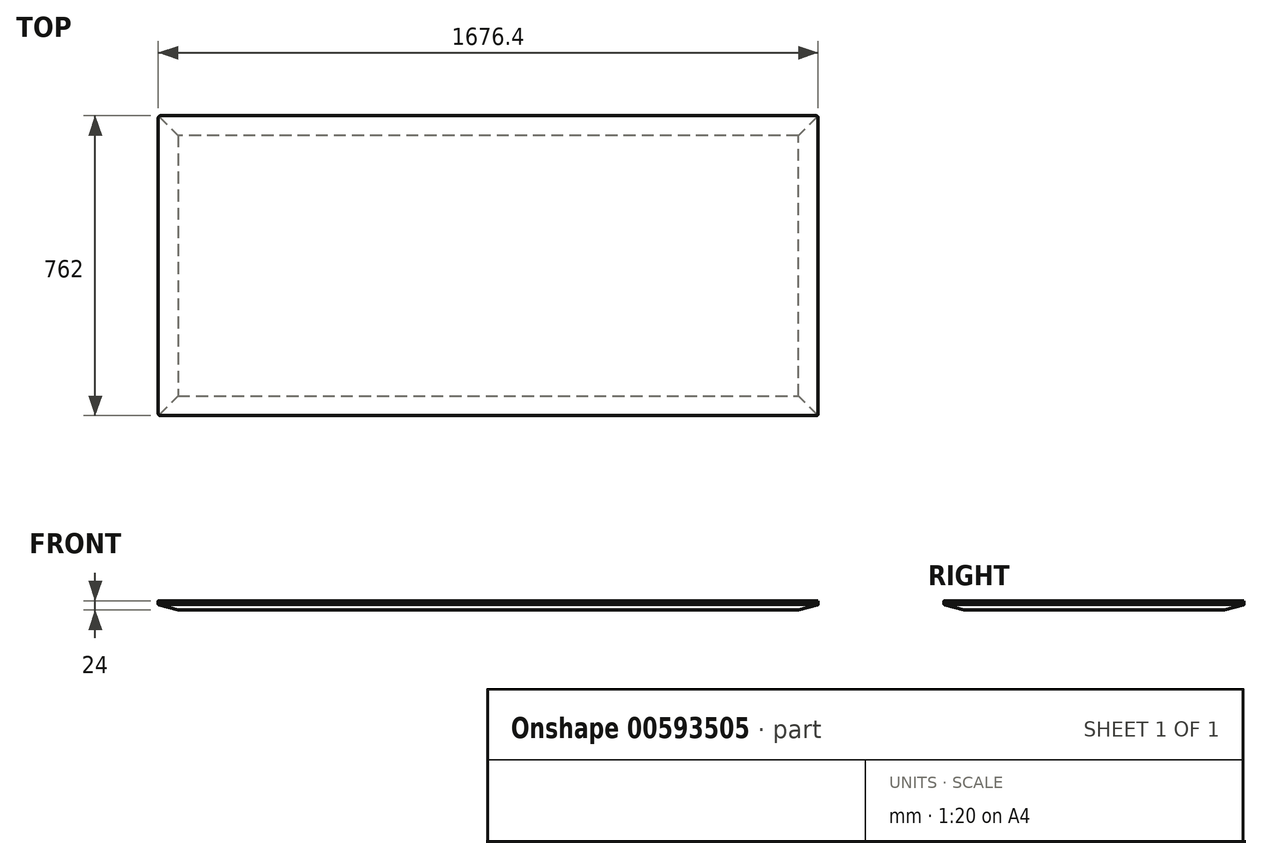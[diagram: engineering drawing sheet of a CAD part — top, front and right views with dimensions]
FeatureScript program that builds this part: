
annotation { "Feature Type Name" : "Feature", "Feature Type Description" : "" }
export const myFeature = defineFeature(function(context is Context, id is Id, definition is map)
    precondition{}
    {
        {
            var Q0;
            Q0=qCreatedBy(makeId("Top.planeOp"),FACE);
            var sketch = newSketch(context, id + "F0", { "sketchPlane" : qUnion([Q0])});
            skLineSegment(sketch, "E0.bottom", {"start": v(838.2, 381) * mm, "end": v(-838.2, 381) * mm});
            skLineSegment(sketch, "E0.top", {"start": v(838.2, -381) * mm, "end": v(-838.2, -381) * mm});
            skLineSegment(sketch, "E0.left", {"start": v(838.2, 381) * mm, "end": v(838.2, -381) * mm});
            skLineSegment(sketch, "E0.right", {"start": v(-838.2, 381) * mm, "end": v(-838.2, -381) * mm});
            skPoint(sketch, "E0.middle", {"position": v(0, 0) * mm});
            skSolve(sketch);
        }
        {
            var Q0;
            Q0 = qSketchRegion(id + "F0", true);
            extrude(context, id + "F1", {"entities" : qUnion([Q0]), "depth" : 24 * mm, "offsetDistance" : 25.4 * mm});
        }
        {
            var Q0;
            Q0=makeQuery(id+"F1.opExtrude","SWEPT_FACE",FACE,{"disambiguationData":[OSD([sQuery(id+"F0.wireOp",EDGE,"E0.left")])]});
            var sketch = newSketch(context, id + "F2", { "sketchPlane" : qUnion([Q0])});
            skLineSegment(sketch, "E1", {"start": v(331, 0) * mm, "end": v(381, 14) * mm});
            skLineSegment(sketch, "E2", {"start": v(381, 14) * mm, "end": v(381, 0) * mm});
            skLineSegment(sketch, "E3", {"start": v(381, 0) * mm, "end": v(331, 0) * mm});
            skSolve(sketch);
        }
        {
            var Q0;
            Q0=makeQuery(id+"F1.opExtrude","CAP_FACE",FACE,{"disambiguationData":[OSD([sQuery(id+"F0.wireOp",EDGE,"E0.bottom"),sQuery(id+"F0.wireOp",EDGE,"E0.top"),sQuery(id+"F0.wireOp",EDGE,"E0.left"),sQuery(id+"F0.wireOp",EDGE,"E0.right")])],"isStart":true});
            var sketch = newSketch(context, id + "F3", { "sketchPlane" : qUnion([Q0])});
            skLineSegment(sketch, "E4.0.0", {"start": v(838.2, 381) * mm, "end": v(-838.2, 381) * mm});
            skLineSegment(sketch, "E4.0.1", {"start": v(-838.2, 381) * mm, "end": v(-838.2, -381) * mm});
            skLineSegment(sketch, "E4.0.2", {"start": v(-838.2, -381) * mm, "end": v(838.2, -381) * mm});
            skLineSegment(sketch, "E4.0.3", {"start": v(838.2, -381) * mm, "end": v(838.2, 381) * mm});
            skSolve(sketch);
        }
        {
            var Q0;
            Q0 = qSketchRegion(id + "F2", true);
            var Q1;
            Q1 = qConstructionFilter(qBodyType(qCreatedBy(id + "F3" ,EDGE), BodyType.WIRE), ConstructionObject.NO);
            sweep(context, id + "F4", {"operationType" : NewBodyOperationType.REMOVE, "profiles" : qUnion([Q0]), "path" : qUnion([Q1])});
        }
        {
            var Q0;
            Q0=makeQuery(id+"F1.opExtrude","SWEPT_EDGE",EDGE,{"disambiguationData":[OSD([sQuery(id+"F0.wireOp",EDGE,"E0.bottom"),sQuery(id+"F0.wireOp",EDGE,"E0.left")])]});
            var Q1;
            Q1=makeQuery(id+"F1.opExtrude","SWEPT_EDGE",EDGE,{"disambiguationData":[OSD([sQuery(id+"F0.wireOp",EDGE,"E0.top"),sQuery(id+"F0.wireOp",EDGE,"E0.left")])]});
            var Q2;
            Q2=makeQuery(id+"F1.opExtrude","SWEPT_EDGE",EDGE,{"disambiguationData":[OSD([sQuery(id+"F0.wireOp",EDGE,"E0.bottom"),sQuery(id+"F0.wireOp",EDGE,"E0.right")])]});
            var Q3;
            Q3=makeQuery(id+"F1.opExtrude","SWEPT_EDGE",EDGE,{"disambiguationData":[OSD([sQuery(id+"F0.wireOp",EDGE,"E0.top"),sQuery(id+"F0.wireOp",EDGE,"E0.right")])]});
            fillet(context, id + "F5", {"entities" : qUnion([Q0, Q1, Q2, Q3]), "radius" : 5 * mm, "tangentPropagation" : true, "allowEdgeOverflow" : false});
        }
    });
